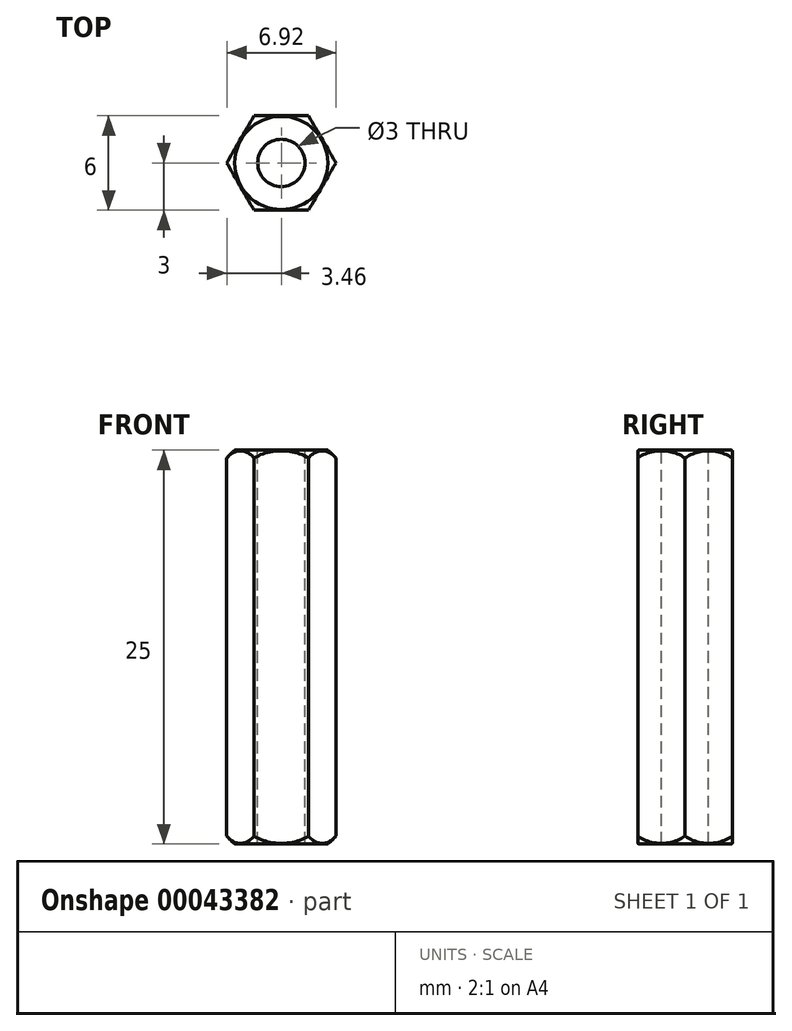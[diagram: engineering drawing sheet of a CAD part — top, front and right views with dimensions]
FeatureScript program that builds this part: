
annotation { "Feature Type Name" : "Feature", "Feature Type Description" : "" }
export const myFeature = defineFeature(function(context is Context, id is Id, definition is map)
    precondition{}
    {
        {
            var Q0;
            Q0=qCreatedBy(makeId("Top.planeOp"),FACE);
            var sketch = newSketch(context, id + "F0", { "sketchPlane" : qUnion([Q0])});
            skCircle(sketch, "E0.cCircle", {"center": v(0, 0) * mm, "radius": 3 * mm, "construction": true});
            skLineSegment(sketch, "E0.0", {"start": v(1.73, 3) * mm, "end": v(3.46, 0) * mm});
            skLineSegment(sketch, "E0.1", {"start": v(3.46, 0) * mm, "end": v(1.73, -3) * mm});
            skLineSegment(sketch, "E0.2", {"start": v(1.73, -3) * mm, "end": v(-1.73, -3) * mm});
            skLineSegment(sketch, "E0.3", {"start": v(-1.73, -3) * mm, "end": v(-3.46, 0) * mm});
            skLineSegment(sketch, "E0.4", {"start": v(-3.46, 0) * mm, "end": v(-1.73, 3) * mm});
            skLineSegment(sketch, "E0.5", {"start": v(-1.73, 3) * mm, "end": v(1.73, 3) * mm});
            skPoint(sketch, "E0.0.midPoint", {"position": v(2.6, 1.5) * mm});
            skSolve(sketch);
        }
        {
            var Q0;
            Q0=qSketchRegion(id+"F0",true);
            extrude(context, id + "F1", {"entities" : qUnion([Q0]), "depth" : 25 * mm});
        }
        {
            var Q0;
            Q0=qCreatedBy(makeId("Front.planeOp"),FACE);
            var sketch = newSketch(context, id + "F2", { "sketchPlane" : qUnion([Q0])});
            skLineSegment(sketch, "E1", {"start": v(0, 25) * mm, "end": v(0, 0) * mm, "construction": true});
            skLineSegment(sketch, "E2", {"start": v(0, 25.5) * mm, "end": v(1.43, 25.5) * mm});
            skLineSegment(sketch, "E3", {"start": v(3.97, 22.97) * mm, "end": v(3.97, 22) * mm});
            skLineSegment(sketch, "E4", {"start": v(3.97, 22) * mm, "end": v(5.78, 22) * mm});
            skLineSegment(sketch, "E5", {"start": v(5.78, 22) * mm, "end": v(5.78, 27.3) * mm});
            skLineSegment(sketch, "E6", {"start": v(5.78, 27.3) * mm, "end": v(0, 27.3) * mm});
            skLineSegment(sketch, "E7", {"start": v(0, 27.3) * mm, "end": v(0, 25.5) * mm});
            skPoint(sketch, "E8.visualSharp", {"position": v(3.97, 25.5) * mm});
            skArc(sketch, "E8.filletArc", {"start": v(3.97, 22.97) * mm, "mid": v(3.23, 24.76) * mm, "end": v(1.43, 25.5) * mm});
            skPoint(sketch, "E9", {"position": v(0, 12.5) * mm});
            skLineSegment(sketch, "E10", {"start": v(0, 12.5) * mm, "end": v(11.8, 12.5) * mm, "construction": true});
            skLineSegment(sketch, "E11.MirrorCS", {"start": v(0, -2.3) * mm, "end": v(0, -0.5) * mm});
            skLineSegment(sketch, "E12.MirrorCS", {"start": v(3.97, 2.03) * mm, "end": v(3.97, 3) * mm});
            skLineSegment(sketch, "E13.MirrorCS", {"start": v(3.97, 3) * mm, "end": v(5.78, 3) * mm});
            skLineSegment(sketch, "E14.MirrorCS", {"start": v(0, -0.5) * mm, "end": v(1.43, -0.5) * mm});
            skArc(sketch, "E15.MirrorCS", {"start": v(3.97, 2.03) * mm, "mid": v(3.23, 0.24) * mm, "end": v(1.43, -0.5) * mm});
            skLineSegment(sketch, "E16.MirrorCS", {"start": v(5.78, -2.3) * mm, "end": v(0, -2.3) * mm});
            skLineSegment(sketch, "E17.MirrorCS", {"start": v(5.78, 3) * mm, "end": v(5.78, -2.3) * mm});
            skPoint(sketch, "E18.MirrorP", {"position": v(3.97, -0.5) * mm});
            skSolve(sketch);
        }
        {
            var Q0;
            Q0=qSketchRegion(id+"F2",true);
            var Q1;
            Q1=sQuery(id+"F2.wireOp",EDGE,"E1");
            revolve(context, id + "F3", {"operationType" : NewBodyOperationType.REMOVE, "entities" : qUnion([Q0]), "axis" : qUnion([Q1]), "revolveType" : RevolveType.FULL, "oppositeDirection" : true});
        }
        {
            var Q0;
            Q0=makeQuery(id+"F1.opExtrude","CAP_FACE",FACE,{"disambiguationData":[OSD([sQuery(id+"F0.wireOp",EDGE,"E0.0"),sQuery(id+"F0.wireOp",EDGE,"E0.1"),sQuery(id+"F0.wireOp",EDGE,"E0.2"),sQuery(id+"F0.wireOp",EDGE,"E0.3"),sQuery(id+"F0.wireOp",EDGE,"E0.4"),sQuery(id+"F0.wireOp",EDGE,"E0.5")])],"isStart":false});
            var sketch = newSketch(context, id + "F4", { "sketchPlane" : qUnion([Q0])});
            skPoint(sketch, "E19", {"position": v(0, 0) * mm});
            skSolve(sketch);
        }
        {
            var Q0;
            Q0=sQuery(id+"F4.wireOp",VERTEX,"E19");
            var Q1;
            Q1=makeQuery(id+"F1.opExtrude","SWEPT_BODY",BODY,{"disambiguationData":[OSD([sQuery(id+"F0.wireOp",EDGE,"E0.0"),sQuery(id+"F0.wireOp",EDGE,"E0.1"),sQuery(id+"F0.wireOp",EDGE,"E0.2"),sQuery(id+"F0.wireOp",EDGE,"E0.3"),sQuery(id+"F0.wireOp",EDGE,"E0.4"),sQuery(id+"F0.wireOp",EDGE,"E0.5")])]});
            hole(context, id + "F5", {"style" : HoleStyle.SIMPLE, "holeDiameter" : 3 * mm, "endStyle" : HoleEndStyle.BLIND, "holeDepth" : 12.7 * mm, "locations" : qUnion([Q0]), "scope" : qUnion([Q1])});
        }
        {
            var Q0;
            Q0=makeQuery(id+"F1.opExtrude","CAP_FACE",FACE,{"disambiguationData":[OSD([sQuery(id+"F0.wireOp",EDGE,"E0.0"),sQuery(id+"F0.wireOp",EDGE,"E0.1"),sQuery(id+"F0.wireOp",EDGE,"E0.2"),sQuery(id+"F0.wireOp",EDGE,"E0.3"),sQuery(id+"F0.wireOp",EDGE,"E0.4"),sQuery(id+"F0.wireOp",EDGE,"E0.5")])],"isStart":true});
            var sketch = newSketch(context, id + "F6", { "sketchPlane" : qUnion([Q0])});
            skPoint(sketch, "E20", {"position": v(0, 0) * mm});
            skSolve(sketch);
        }
        {
            var Q0;
            Q0=sQuery(id+"F6.wireOp",VERTEX,"E20");
            var Q1;
            Q1=makeQuery(id+"F1.opExtrude","SWEPT_BODY",BODY,{"disambiguationData":[OSD([sQuery(id+"F0.wireOp",EDGE,"E0.0"),sQuery(id+"F0.wireOp",EDGE,"E0.1"),sQuery(id+"F0.wireOp",EDGE,"E0.2"),sQuery(id+"F0.wireOp",EDGE,"E0.3"),sQuery(id+"F0.wireOp",EDGE,"E0.4"),sQuery(id+"F0.wireOp",EDGE,"E0.5")])]});
            hole(context, id + "F7", {"style" : HoleStyle.SIMPLE, "holeDiameter" : 3 * mm, "endStyle" : HoleEndStyle.BLIND, "holeDepth" : 12.7 * mm, "locations" : qUnion([Q0]), "scope" : qUnion([Q1])});
        }
    });
